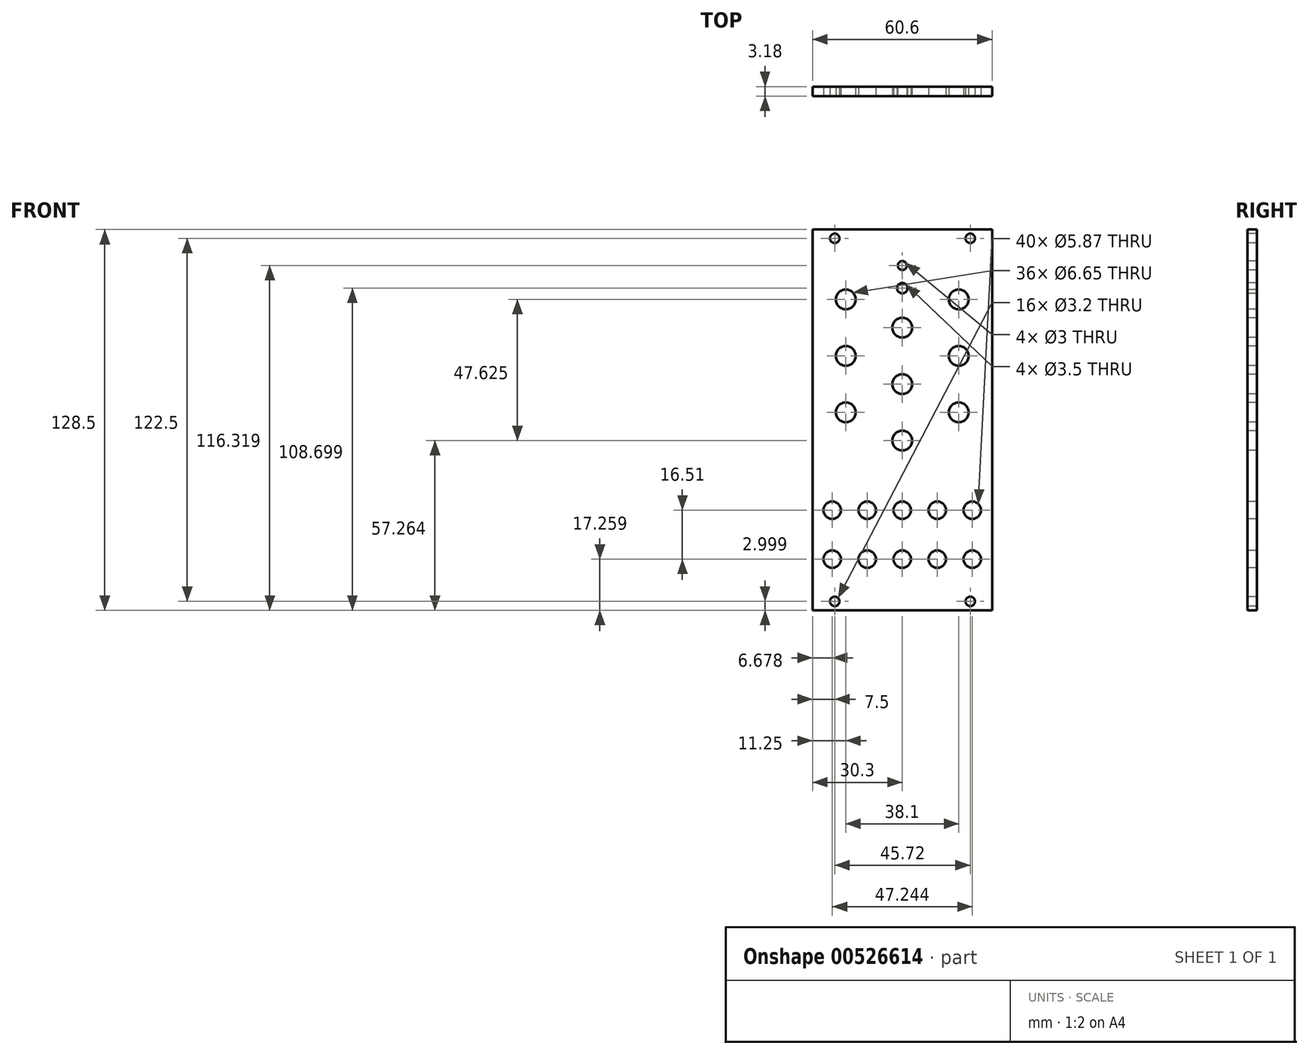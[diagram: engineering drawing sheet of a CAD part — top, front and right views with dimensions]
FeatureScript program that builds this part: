
annotation { "Feature Type Name" : "Feature", "Feature Type Description" : "" }
export const myFeature = defineFeature(function(context is Context, id is Id, definition is map)
    precondition{}
    {
        {
            var Q0;
            Q0=qCreatedBy(makeId("Front.planeOp"),FACE);
            var sketch = newSketch(context, id + "F0", { "sketchPlane" : qUnion([Q0])});
            skLineSegment(sketch, "E0.bottom", {"start": v(-30.3, 72.47) * mm, "end": v(30.3, 72.47) * mm});
            skLineSegment(sketch, "E0.top", {"start": v(-30.3, -56.03) * mm, "end": v(30.3, -56.03) * mm});
            skLineSegment(sketch, "E0.left", {"start": v(-30.3, 72.47) * mm, "end": v(-30.3, -56.03) * mm});
            skLineSegment(sketch, "E0.right", {"start": v(30.3, 72.47) * mm, "end": v(30.3, -56.03) * mm});
            skSolve(sketch);
        }
        {
            var Q0;
            Q0 = qSketchRegion(id + "F0", true);
            extrude(context, id + "F1", {"entities" : qUnion([Q0]), "depth" : 3.17 * mm, "offsetDistance" : 25.4 * mm});
        }
        {
            var Q0;
            Q0=makeQuery(id+"F1.opExtrude","CAP_FACE",FACE,{"disambiguationData":[OSD([sQuery(id+"F0.wireOp",EDGE,"E0.bottom"),sQuery(id+"F0.wireOp",EDGE,"E0.top"),sQuery(id+"F0.wireOp",EDGE,"E0.left"),sQuery(id+"F0.wireOp",EDGE,"E0.right")])],"isStart":false});
            var sketch = newSketch(context, id + "F2", { "sketchPlane" : qUnion([Q0])});
            skPoint(sketch, "E1", {"position": v(-22.8, -53.03) * mm});
            skPoint(sketch, "E2", {"position": v(22.92, -53.03) * mm});
            skPoint(sketch, "E3", {"position": v(-22.8, 69.47) * mm});
            skPoint(sketch, "E4", {"position": v(22.92, 69.47) * mm});
            skSolve(sketch);
        }
        {
            var Q0;
            Q0=sQuery(id+"F2.wireOp",VERTEX,"E1");
            var Q1;
            Q1=sQuery(id+"F2.wireOp",VERTEX,"E2");
            var Q2;
            Q2=sQuery(id+"F2.wireOp",VERTEX,"E4");
            var Q3;
            Q3=sQuery(id+"F2.wireOp",VERTEX,"E3");
            var Q4;
            Q4=makeQuery(id+"F1.opExtrude","SWEPT_BODY",BODY,{"disambiguationData":[OSD([sQuery(id+"F0.wireOp",EDGE,"E0.bottom"),sQuery(id+"F0.wireOp",EDGE,"E0.top"),sQuery(id+"F0.wireOp",EDGE,"E0.left"),sQuery(id+"F0.wireOp",EDGE,"E0.right")])]});
            hole(context, id + "F3", {"style" : HoleStyle.SIMPLE, "endStyle" : HoleEndStyle.THROUGH, "holeDiameter" : 3.2 * mm, "isTappedThrough" : true, "tappedDepth" : 12.7 * mm, "tapClearance" : 3, "locations" : qUnion([Q0, Q1, Q2, Q3]), "scope" : qUnion([Q4])});
        }
        {
            var Q0;
            Q0=makeQuery(id+"F1.opExtrude","CAP_FACE",FACE,{"disambiguationData":[OSD([sQuery(id+"F0.wireOp",EDGE,"E0.bottom"),sQuery(id+"F0.wireOp",EDGE,"E0.top"),sQuery(id+"F0.wireOp",EDGE,"E0.left"),sQuery(id+"F0.wireOp",EDGE,"E0.right")])],"isStart":false});
            var sketch = newSketch(context, id + "F4", { "sketchPlane" : qUnion([Q0])});
            skLineSegment(sketch, "E5.bottom", {"start": v(-29.84, 62.2) * mm, "end": v(29.84, 62.2) * mm, "construction": true});
            skLineSegment(sketch, "E5.top", {"start": v(-29.84, -45.76) * mm, "end": v(29.84, -45.76) * mm, "construction": true});
            skLineSegment(sketch, "E5.left", {"start": v(-29.84, 62.2) * mm, "end": v(-29.85, -45.76) * mm, "construction": true});
            skLineSegment(sketch, "E5.right", {"start": v(29.85, 62.2) * mm, "end": v(29.84, -45.76) * mm, "construction": true});
            skPoint(sketch, "E6", {"position": v(0, -45.76) * mm});
            skPoint(sketch, "E7", {"position": v(29.85, 8.22) * mm});
            skPoint(sketch, "E8", {"position": v(-23.62, -38.77) * mm});
            skPoint(sketch, "E9.0.1.0", {"position": v(-23.62, -22.26) * mm});
            skPoint(sketch, "E9.1.0.0", {"position": v(-11.81, -38.77) * mm});
            skPoint(sketch, "E9.1.1.0", {"position": v(-11.81, -22.26) * mm});
            skPoint(sketch, "E9.2.0.0", {"position": v(0, -38.77) * mm});
            skPoint(sketch, "E9.2.1.0", {"position": v(0, -22.26) * mm});
            skPoint(sketch, "E9.3.0.0", {"position": v(11.81, -38.77) * mm});
            skPoint(sketch, "E9.3.1.0", {"position": v(11.81, -22.26) * mm});
            skLineSegment(sketch, "E9.direction1", {"start": v(-23.62, -38.77) * mm, "end": v(-11.81, -38.77) * mm, "construction": true});
            skLineSegment(sketch, "E9.direction2", {"start": v(-23.62, -38.77) * mm, "end": v(-23.62, -22.26) * mm, "construction": true});
            skPoint(sketch, "E10.0.4.0", {"position": v(23.62, -38.77) * mm});
            skPoint(sketch, "E10.0.4.1", {"position": v(23.62, -22.26) * mm});
            skPoint(sketch, "E11", {"position": v(-19.05, 48.86) * mm});
            skPoint(sketch, "E12.0.1.0", {"position": v(-19.05, 39.33) * mm});
            skPoint(sketch, "E12.0.2.0", {"position": v(-19.05, 29.8) * mm});
            skPoint(sketch, "E12.1.0.0", {"position": v(0, 48.86) * mm});
            skPoint(sketch, "E12.1.1.0", {"position": v(0, 39.33) * mm});
            skPoint(sketch, "E12.1.2.0", {"position": v(0, 29.8) * mm});
            skPoint(sketch, "E12.2.0.0", {"position": v(19.05, 48.86) * mm});
            skPoint(sketch, "E12.2.1.0", {"position": v(19.05, 39.33) * mm});
            skPoint(sketch, "E12.2.2.0", {"position": v(19.05, 29.8) * mm});
            skLineSegment(sketch, "E12.direction1", {"start": v(-19.05, 48.86) * mm, "end": v(0, 48.86) * mm, "construction": true});
            skLineSegment(sketch, "E12.direction2", {"start": v(-19.05, 48.86) * mm, "end": v(-19.05, 39.33) * mm, "construction": true});
            skPoint(sketch, "E13.0.0.3", {"position": v(-19.05, 20.28) * mm});
            skPoint(sketch, "E13.0.0.4", {"position": v(-19.05, 10.76) * mm});
            skPoint(sketch, "E13.0.0.5", {"position": v(-19.05, 1.23) * mm});
            skPoint(sketch, "E13.0.1.3", {"position": v(0, 20.28) * mm});
            skPoint(sketch, "E13.0.1.4", {"position": v(0, 10.76) * mm});
            skPoint(sketch, "E13.0.1.5", {"position": v(0, 1.23) * mm});
            skPoint(sketch, "E13.0.2.3", {"position": v(19.05, 20.28) * mm});
            skPoint(sketch, "E13.0.2.4", {"position": v(19.05, 10.76) * mm});
            skPoint(sketch, "E13.0.2.5", {"position": v(19.05, 1.23) * mm});
            skPoint(sketch, "E14", {"position": v(0, 52.67) * mm});
            skPoint(sketch, "E15", {"position": v(0, 60.29) * mm});
            skSolve(sketch);
        }
        {
            var Q0;
            Q0=sQuery(id+"F4.wireOp",VERTEX,"E8");
            var Q1;
            Q1=sQuery(id+"F4.wireOp",VERTEX,"E9.0.1.0");
            var Q2;
            Q2=sQuery(id+"F4.wireOp",VERTEX,"E9.1.1.0");
            var Q3;
            Q3=sQuery(id+"F4.wireOp",VERTEX,"E9.1.0.0");
            var Q4;
            Q4=sQuery(id+"F4.wireOp",VERTEX,"E9.2.1.0");
            var Q5;
            Q5=sQuery(id+"F4.wireOp",VERTEX,"E9.2.0.0");
            var Q6;
            Q6=sQuery(id+"F4.wireOp",VERTEX,"E9.3.1.0");
            var Q7;
            Q7=sQuery(id+"F4.wireOp",VERTEX,"E9.3.0.0");
            var Q8;
            Q8=sQuery(id+"F4.wireOp",VERTEX,"E10.0.4.1");
            var Q9;
            Q9=sQuery(id+"F4.wireOp",VERTEX,"E10.0.4.0");
            var Q10;
            Q10=makeQuery(id+"F1.opExtrude","SWEPT_BODY",BODY,{"disambiguationData":[OSD([sQuery(id+"F0.wireOp",EDGE,"E0.bottom"),sQuery(id+"F0.wireOp",EDGE,"E0.top"),sQuery(id+"F0.wireOp",EDGE,"E0.left"),sQuery(id+"F0.wireOp",EDGE,"E0.right")])]});
            hole(context, id + "F5", {"style" : HoleStyle.SIMPLE, "endStyle" : HoleEndStyle.THROUGH, "holeDiameter" : 5.87 * mm, "isTappedThrough" : true, "tappedDepth" : 12.7 * mm, "tapClearance" : 3, "locations" : qUnion([Q0, Q1, Q2, Q3, Q4, Q5, Q6, Q7, Q8, Q9]), "scope" : qUnion([Q10])});
        }
        {
            var Q0;
            Q0=sQuery(id+"F4.wireOp",VERTEX,"E11");
            var Q1;
            Q1=sQuery(id+"F4.wireOp",VERTEX,"E12.1.1.0");
            var Q2;
            Q2=sQuery(id+"F4.wireOp",VERTEX,"E12.2.0.0");
            var Q3;
            Q3=sQuery(id+"F4.wireOp",VERTEX,"E12.0.2.0");
            var Q4;
            Q4=sQuery(id+"F4.wireOp",VERTEX,"E13.0.1.3");
            var Q5;
            Q5=sQuery(id+"F4.wireOp",VERTEX,"E12.2.2.0");
            var Q6;
            Q6=sQuery(id+"F4.wireOp",VERTEX,"E13.0.0.4");
            var Q7;
            Q7=sQuery(id+"F4.wireOp",VERTEX,"E13.0.1.5");
            var Q8;
            Q8=sQuery(id+"F4.wireOp",VERTEX,"E13.0.2.4");
            var Q9;
            Q9=makeQuery(id+"F1.opExtrude","SWEPT_BODY",BODY,{"disambiguationData":[OSD([sQuery(id+"F0.wireOp",EDGE,"E0.bottom"),sQuery(id+"F0.wireOp",EDGE,"E0.top"),sQuery(id+"F0.wireOp",EDGE,"E0.left"),sQuery(id+"F0.wireOp",EDGE,"E0.right")])]});
            hole(context, id + "F6", {"style" : HoleStyle.SIMPLE, "endStyle" : HoleEndStyle.THROUGH, "holeDiameter" : 6.65 * mm, "isTappedThrough" : true, "tappedDepth" : 12.7 * mm, "tapClearance" : 3, "locations" : qUnion([Q0, Q1, Q2, Q3, Q4, Q5, Q6, Q7, Q8]), "scope" : qUnion([Q9])});
        }
        {
            var Q0;
            Q0=sQuery(id+"F4.wireOp",VERTEX,"E15");
            var Q1;
            Q1=makeQuery(id+"F1.opExtrude","SWEPT_BODY",BODY,{"disambiguationData":[OSD([sQuery(id+"F0.wireOp",EDGE,"E0.bottom"),sQuery(id+"F0.wireOp",EDGE,"E0.top"),sQuery(id+"F0.wireOp",EDGE,"E0.left"),sQuery(id+"F0.wireOp",EDGE,"E0.right")])]});
            hole(context, id + "F7", {"style" : HoleStyle.SIMPLE, "endStyle" : HoleEndStyle.THROUGH, "holeDiameter" : 3 * mm, "isTappedThrough" : true, "tappedDepth" : 12.7 * mm, "tapClearance" : 3, "locations" : qUnion([Q0]), "scope" : qUnion([Q1])});
        }
        {
            var Q0;
            Q0=sQuery(id+"F4.wireOp",VERTEX,"E14");
            var Q1;
            Q1=makeQuery(id+"F1.opExtrude","SWEPT_BODY",BODY,{"disambiguationData":[OSD([sQuery(id+"F0.wireOp",EDGE,"E0.bottom"),sQuery(id+"F0.wireOp",EDGE,"E0.top"),sQuery(id+"F0.wireOp",EDGE,"E0.left"),sQuery(id+"F0.wireOp",EDGE,"E0.right")])]});
            hole(context, id + "F8", {"style" : HoleStyle.SIMPLE, "endStyle" : HoleEndStyle.THROUGH, "holeDiameter" : 3.5 * mm, "isTappedThrough" : true, "tappedDepth" : 12.7 * mm, "tapClearance" : 3, "locations" : qUnion([Q0]), "scope" : qUnion([Q1])});
        }
    });
